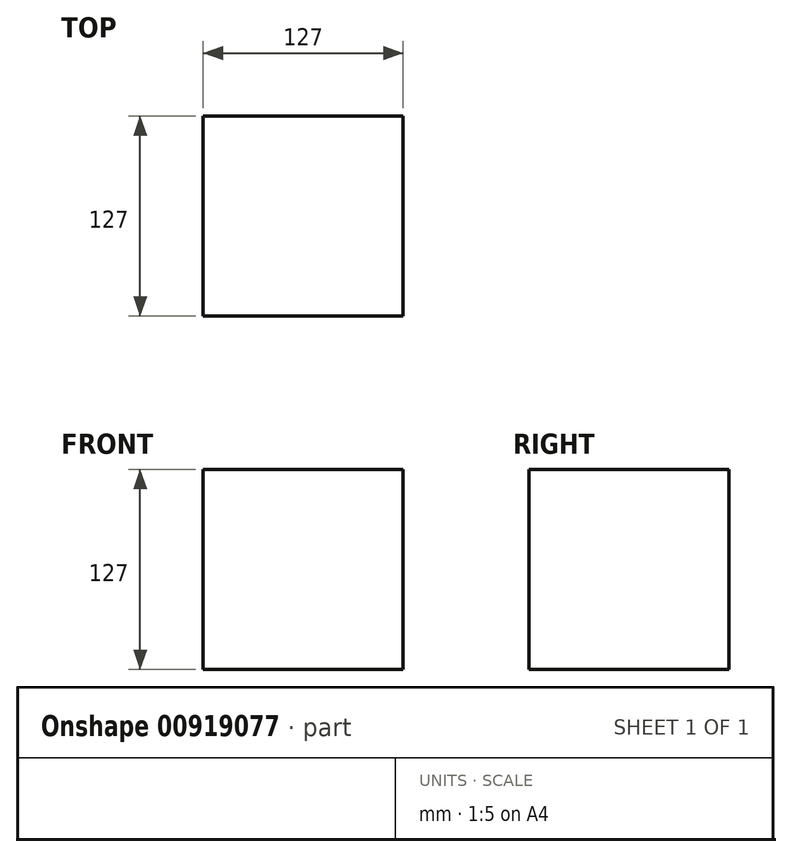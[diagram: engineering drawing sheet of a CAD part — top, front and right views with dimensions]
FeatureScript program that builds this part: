
annotation { "Feature Type Name" : "Feature", "Feature Type Description" : "" }
export const myFeature = defineFeature(function(context is Context, id is Id, definition is map)
    precondition{}
    {
        {
            var Q0;
            Q0=qCreatedBy(makeId("Top.planeOp"),FACE);
            var sketch = newSketch(context, id + "F0", { "sketchPlane" : qUnion([Q0])});
            skLineSegment(sketch, "E0.bottom", {"start": v(63.5, -63.5) * mm, "end": v(-63.5, -63.5) * mm});
            skLineSegment(sketch, "E0.top", {"start": v(63.5, 63.5) * mm, "end": v(-63.5, 63.5) * mm});
            skLineSegment(sketch, "E0.left", {"start": v(63.5, -63.5) * mm, "end": v(63.5, 63.5) * mm});
            skLineSegment(sketch, "E0.right", {"start": v(-63.5, -63.5) * mm, "end": v(-63.5, 63.5) * mm});
            skPoint(sketch, "E0.middle", {"position": v(0, 0) * mm});
            skSolve(sketch);
        }
        {
            var Q0;
            Q0 = qSketchRegion(id + "F0", true);
            extrude(context, id + "F1", {"entities" : qUnion([Q0]), "depth" : 127 * mm, "offsetDistance" : 25.4 * mm});
        }
    });
